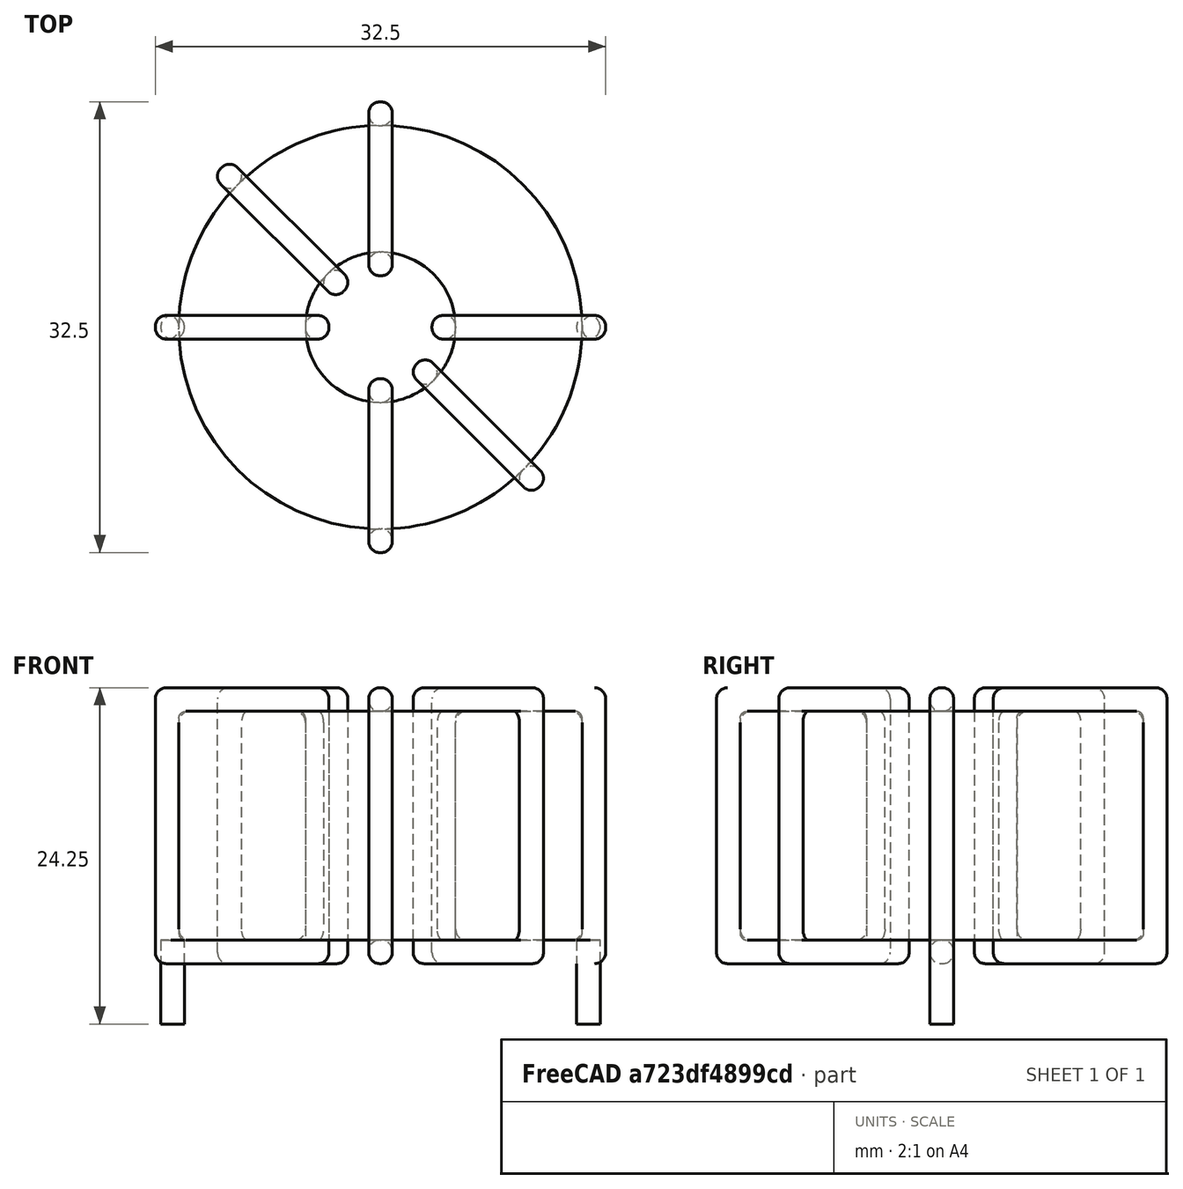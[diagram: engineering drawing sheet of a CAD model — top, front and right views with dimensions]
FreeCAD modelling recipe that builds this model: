
FCSTD DOCUMENT  (FreeCAD 0.16R6703 (Git))
Label: L_Toroid_Horizontal_D32.5mm_P30.00mm_Bourns_2300series
License: All rights reserved
LicenseURL: http://en.wikipedia.org/wiki/All_rights_reserved
objects: Sketcher::SketchObject×6, PartDesign::Pad×6, PartDesign::Fillet×5, Spreadsheet::Sheet×1
note: 23 computed .brp shape members not serialized (recipe doc carries the construction recipe); baked Part::Feature solids carry a one-line shape summary decoded from their .brp

FEATURE [Spreadsheet::Sheet] Spreadsheet  label="dimensions"
  cells = A1=Wx; B1(Wx)=32.5; C1(WW)=10.83333333333333; D1=32.5; A2=Wy; B2(Wy)=32.5; D2=32.5; A3=RM; B3(RMx)=30; C3(RMy)=0; A4=d_wire; B4(d_wire)=1.7; A5=H; B5(H)=16.5; A6=offsetx; B6(offsetx)=1.25
FEATURE [Sketcher::SketchObject] Sketch
  Placement = pos=(0,0,2.2) rot=(0,0,1;0rad)
  expr: Placement.Base.z = 0.5 + Spreadsheet.d_wire
  expr: Constraints[0] = Spreadsheet.Wx / 2 - Spreadsheet.d_wire
  expr: Constraints[4] = Spreadsheet.WW / 2
  expr: Constraints[2] = Spreadsheet.RMy / 2
  expr: Constraints[1] = Spreadsheet.RMx / 2
  sketch-geometry (2):
    g0: Circle CenterX=15 CenterY=0 CenterZ=0 NormalX=0 NormalY=0 NormalZ=1 Radius=14.55
    g1: Circle CenterX=15 CenterY=0 CenterZ=0 NormalX=0 NormalY=0 NormalZ=1 Radius=5.41667
  constraints (5):
    c: Radius(g0) = 14.55
    c: DistanceX(g-1,g0) = 15
    c: DistanceY(g-1,g0) = 0
    c: Coincident(g1,g0)
    c: Radius(g1) = 5.41667
FEATURE [PartDesign::Pad] Pad
  Length = 16.5
  Length2 = 100
  Placement = pos=(0,0,2.2) rot=(0,0,1;0rad)
  Sketch = -> Sketch
  Type = 0
  expr: Length = Spreadsheet.H
FEATURE [Sketcher::SketchObject] Sketch001
  Placement = pos=(0,0,1.35) rot=(0,0,1;0rad)
  expr: Placement.Base.z = 0.5 + Spreadsheet.d_wire * 0.5
  expr: Constraints[4] = Spreadsheet.RMx
  expr: Constraints[2] = Spreadsheet.RMy
  expr: Constraints[1] = Spreadsheet.d_wire / 2
  sketch-geometry (2):
    g0: Circle CenterX=0 CenterY=0 CenterZ=0 NormalX=0 NormalY=0 NormalZ=1 Radius=0.85
    g1: Circle CenterX=30 CenterY=0 CenterZ=0 NormalX=0 NormalY=0 NormalZ=1 Radius=0.85
  constraints (5):
    c: Equal(g0,g1)
    c: Radius(g0) = 0.85
    c: DistanceY(g-1,g1) = 0
    c: Coincident(g0,g-1)
    c: DistanceX(g-1,g1) = 30
FEATURE [PartDesign::Pad] Pad001
  Length = 0.85
  Length2 = 5.2
  Placement = pos=(0,0,1.35) rot=(0,0,1;0rad)
  Reversed = true
  Sketch = -> Sketch001
  Type = 4
  expr: Length2 = 3.5 + Spreadsheet.d_wire
  expr: Length = Spreadsheet.d_wire / 2
FEATURE [PartDesign::Fillet] Fillet
  Base = -> Pad [Edge6,Edge3,Edge2]
  Placement = pos=(0,0,2.2) rot=(0,0,1;0rad)
  Radius = 0.5
FEATURE [Sketcher::SketchObject] Sketch003
  Placement = pos=(15,0,0) rot=(1,0,0;1.5708rad)
  expr: Placement.Base.x = Spreadsheet.RMx / 2
  expr: Constraints[49] = Spreadsheet.Wx - Spreadsheet.d_wire * 2
  expr: Constraints[44] = Spreadsheet.d_wire
  expr: Constraints[23] = Spreadsheet.H
  expr: Constraints[22] = Spreadsheet.Wx / 2 - Spreadsheet.d_wire
  expr: Placement.Base.y = Spreadsheet.RMy / 2
  expr: Constraints[21] = (Spreadsheet.Wx - Spreadsheet.WW) / 2 - Spreadsheet.d_wire
  expr: Constraints[19] = Spreadsheet.d_wire
  expr: Constraints[17] = Spreadsheet.d_wire
  expr: Constraints[18] = Spreadsheet.d_wire
  expr: Constraints[16] = Spreadsheet.d_wire
  sketch-geometry (16):
    g0: LineSegment StartX=-3.71667 StartY=0.5 StartZ=0 EndX=-16.25 EndY=0.5 EndZ=0
    g1: LineSegment StartX=-16.25 StartY=0.5 StartZ=0 EndX=-16.25 EndY=20.4 EndZ=0
    g2: LineSegment StartX=-16.25 StartY=20.4 StartZ=0 EndX=-3.71667 EndY=20.4 EndZ=0
    g3: LineSegment StartX=-3.71667 StartY=20.4 StartZ=0 EndX=-3.71667 EndY=0.5 EndZ=0
    g4: LineSegment StartX=-14.55 StartY=18.7 StartZ=0 EndX=-5.41667 EndY=18.7 EndZ=0
    g5: LineSegment StartX=-5.41667 StartY=18.7 StartZ=0 EndX=-5.41667 EndY=2.2 EndZ=0
    g6: LineSegment StartX=-5.41667 StartY=2.2 StartZ=0 EndX=-14.55 EndY=2.2 EndZ=0
    g7: LineSegment StartX=-14.55 StartY=2.2 StartZ=0 EndX=-14.55 EndY=18.7 EndZ=0
    g8: LineSegment StartX=3.71667 StartY=20.4 StartZ=0 EndX=16.25 EndY=20.4 EndZ=0
    g9: LineSegment StartX=16.25 StartY=20.4 StartZ=0 EndX=16.25 EndY=0.5 EndZ=0
    g10: LineSegment StartX=16.25 StartY=0.5 StartZ=0 EndX=3.71667 EndY=0.5 EndZ=0
    g11: LineSegment StartX=3.71667 StartY=0.5 StartZ=0 EndX=3.71667 EndY=20.4 EndZ=0
    g12: LineSegment StartX=5.41667 StartY=18.7 StartZ=0 EndX=14.55 EndY=18.7 EndZ=0
    g13: LineSegment StartX=14.55 StartY=18.7 StartZ=0 EndX=14.55 EndY=2.2 EndZ=0
    g14: LineSegment StartX=14.55 StartY=2.2 StartZ=0 EndX=5.41667 EndY=2.2 EndZ=0
    g15: LineSegment StartX=5.41667 StartY=2.2 StartZ=0 EndX=5.41667 EndY=18.7 EndZ=0
  constraints (50):
    c: Horizontal(g0)
    c: Coincident(g1,g0)
    c: Vertical(g1)
    c: Coincident(g2,g1)
    c: Horizontal(g2)
    c: Coincident(g3,g2)
    c: Coincident(g3,g0)
    c: Vertical(g3)
    c: Coincident(g4,g5)
    c: Coincident(g5,g6)
    c: Coincident(g6,g7)
    c: Coincident(g7,g4)
    c: Horizontal(g4)
    c: Horizontal(g6)
    c: Vertical(g5)
    c: Vertical(g7)
    c: DistanceX(g1,g4) = 1.7
    c: DistanceY(g4,g1) = 1.7
    c: DistanceX(g5,g0) = 1.7
    c: DistanceY(g0,g5) = 1.7
    c: DistanceY(g-1,g0) = 0.5
    c: DistanceX(g6,g6) = 9.13333
    c: DistanceX(g6,g-1) = 14.55
    c: DistanceY(g7,g7) = 16.5
    c: Coincident(g8,g9)
    c: Coincident(g9,g10)
    c: Coincident(g10,g11)
    c: Coincident(g11,g8)
    c: Horizontal(g8)
    c: Horizontal(g10)
    c: Vertical(g9)
    c: Vertical(g11)
    c: Coincident(g12,g13)
    c: Coincident(g13,g14)
    c: Coincident(g14,g15)
    c: Coincident(g15,g12)
    c: Horizontal(g12)
    c: Horizontal(g14)
    c: Vertical(g13)
    c: Vertical(g15)
    c: DistanceY(g8,g2) = 0
    c: DistanceY(g10,g0) = 0
    c: DistanceY(g14,g5) = 0
    c: DistanceY(g12,g4) = 0
    c: DistanceX(g8,g12) = 1.7
    c: Equal(g8,g2)
    c: Equal(g12,g4)
    c: Equal(g9,g1)
    c: Equal(g13,g7)
    c: DistanceX(g4,g12) = 29.1
FEATURE [PartDesign::Pad] Pad002
  Length = 1.7
  Length2 = 100
  Midplane = true
  Placement = pos=(15,0,0) rot=(1,0,0;1.5708rad)
  Sketch = -> Sketch003
  Type = 0
  expr: Length = Spreadsheet.d_wire
FEATURE [PartDesign::Fillet] Fillet001
  Base = -> Pad002 [Edge38,Edge41,Edge42,Edge43,Edge29,Edge32,Edge33,Edge34,Edge25,Edge35,Edge36,Edge13,Edge14,Edge15,Edge16,Edge17,Edge18,Edge19,Edge1,Edge2,Edge3,Edge4,Edge5,Edge6,Edge7,Edge37,Edge39,Edge40,Edge20,Edge23,Edge24,Edge21,Edge22,Edge8,Edge9,Edge10,Edge11,Edge12,Edge26,Edge27,+8 more]
  Placement = pos=(15,0,0) rot=(1,0,0;1.5708rad)
  Radius = 0.799
  expr: Radius = Spreadsheet.d_wire * 0.47
FEATURE [Sketcher::SketchObject] Sketch004
  Placement = pos=(15,0,0) rot=(0.862856,0.357407,0.357407;1.71777rad)
  expr: Placement.Base.x = Spreadsheet.RMx / 2
  expr: Constraints[49] = Spreadsheet.Wx - 2 * Spreadsheet.d_wire
  expr: Constraints[44] = Spreadsheet.d_wire
  expr: Constraints[23] = Spreadsheet.H
  expr: Constraints[22] = Spreadsheet.Wx / 2 - Spreadsheet.d_wire
  expr: Placement.Base.y = Spreadsheet.RMy / 2
  expr: Constraints[21] = (Spreadsheet.Wx - Spreadsheet.WW) / 2 - Spreadsheet.d_wire
  expr: Constraints[19] = Spreadsheet.d_wire
  expr: Constraints[17] = Spreadsheet.d_wire
  expr: Constraints[18] = Spreadsheet.d_wire
  expr: Constraints[16] = Spreadsheet.d_wire
  sketch-geometry (16):
    g0: LineSegment StartX=-3.71667 StartY=0.5 StartZ=0 EndX=-16.25 EndY=0.5 EndZ=0
    g1: LineSegment StartX=-16.25 StartY=0.5 StartZ=0 EndX=-16.25 EndY=20.4 EndZ=0
    g2: LineSegment StartX=-16.25 StartY=20.4 StartZ=0 EndX=-3.71667 EndY=20.4 EndZ=0
    g3: LineSegment StartX=-3.71667 StartY=20.4 StartZ=0 EndX=-3.71667 EndY=0.5 EndZ=0
    g4: LineSegment StartX=-14.55 StartY=18.7 StartZ=0 EndX=-5.41667 EndY=18.7 EndZ=0
    g5: LineSegment StartX=-5.41667 StartY=18.7 StartZ=0 EndX=-5.41667 EndY=2.2 EndZ=0
    g6: LineSegment StartX=-5.41667 StartY=2.2 StartZ=0 EndX=-14.55 EndY=2.2 EndZ=0
    g7: LineSegment StartX=-14.55 StartY=2.2 StartZ=0 EndX=-14.55 EndY=18.7 EndZ=0
    g8: LineSegment StartX=3.71667 StartY=20.4 StartZ=0 EndX=16.25 EndY=20.4 EndZ=0
    g9: LineSegment StartX=16.25 StartY=20.4 StartZ=0 EndX=16.25 EndY=0.5 EndZ=0
    g10: LineSegment StartX=16.25 StartY=0.5 StartZ=0 EndX=3.71667 EndY=0.5 EndZ=0
    g11: LineSegment StartX=3.71667 StartY=0.5 StartZ=0 EndX=3.71667 EndY=20.4 EndZ=0
    g12: LineSegment StartX=5.41667 StartY=18.7 StartZ=0 EndX=14.55 EndY=18.7 EndZ=0
    g13: LineSegment StartX=14.55 StartY=18.7 StartZ=0 EndX=14.55 EndY=2.2 EndZ=0
    g14: LineSegment StartX=14.55 StartY=2.2 StartZ=0 EndX=5.41667 EndY=2.2 EndZ=0
    g15: LineSegment StartX=5.41667 StartY=2.2 StartZ=0 EndX=5.41667 EndY=18.7 EndZ=0
  constraints (50):
    c: Horizontal(g0)
    c: Coincident(g1,g0)
    c: Vertical(g1)
    c: Coincident(g2,g1)
    c: Horizontal(g2)
    c: Coincident(g3,g2)
    c: Coincident(g3,g0)
    c: Vertical(g3)
    c: Coincident(g4,g5)
    c: Coincident(g5,g6)
    c: Coincident(g6,g7)
    c: Coincident(g7,g4)
    c: Horizontal(g4)
    c: Horizontal(g6)
    c: Vertical(g5)
    c: Vertical(g7)
    c: DistanceX(g1,g4) = 1.7
    c: DistanceY(g4,g1) = 1.7
    c: DistanceX(g5,g0) = 1.7
    c: DistanceY(g0,g5) = 1.7
    c: DistanceY(g-1,g0) = 0.5
    c: DistanceX(g6,g6) = 9.13333
    c: DistanceX(g6,g-1) = 14.55
    c: DistanceY(g7,g7) = 16.5
    c: Coincident(g8,g9)
    c: Coincident(g9,g10)
    c: Coincident(g10,g11)
    c: Coincident(g11,g8)
    c: Horizontal(g8)
    c: Horizontal(g10)
    c: Vertical(g9)
    c: Vertical(g11)
    c: Coincident(g12,g13)
    c: Coincident(g13,g14)
    c: Coincident(g14,g15)
    c: Coincident(g15,g12)
    c: Horizontal(g12)
    c: Horizontal(g14)
    c: Vertical(g13)
    c: Vertical(g15)
    c: DistanceY(g8,g2) = 0
    c: DistanceY(g10,g0) = 0
    c: DistanceY(g14,g5) = 0
    c: DistanceY(g12,g4) = 0
    c: DistanceX(g8,g12) = 1.7
    c: Equal(g8,g2)
    c: Equal(g12,g4)
    c: Equal(g9,g1)
    c: Equal(g13,g7)
    c: DistanceX(g4,g12) = 29.1
FEATURE [PartDesign::Pad] Pad003
  Length = 1.7
  Length2 = 100
  Midplane = true
  Placement = pos=(15,0,0) rot=(0.862856,0.357407,0.357407;1.71777rad)
  Sketch = -> Sketch004
  Type = 0
  expr: Length = Spreadsheet.d_wire
FEATURE [PartDesign::Fillet] Fillet002
  Base = -> Pad003 [Edge38,Edge41,Edge42,Edge43,Edge29,Edge32,Edge33,Edge34,Edge25,Edge35,Edge36,Edge13,Edge14,Edge15,Edge16,Edge17,Edge18,Edge19,Edge1,Edge2,Edge3,Edge4,Edge5,Edge6,Edge7,Edge37,Edge39,Edge40,Edge20,Edge23,Edge24,Edge21,Edge22,Edge8,Edge9,Edge10,Edge11,Edge12,Edge26,Edge27,+8 more]
  Placement = pos=(15,0,0) rot=(0.862856,0.357407,0.357407;1.71777rad)
  Radius = 0.799
  expr: Radius = Spreadsheet.d_wire * 0.47
FEATURE [Sketcher::SketchObject] Sketch005
  Placement = pos=(15,0,0) rot=(0.862856,-0.357407,-0.357407;1.71777rad)
  expr: Placement.Base.x = Spreadsheet.RMx / 2
  expr: Constraints[49] = Spreadsheet.Wx - 2 * Spreadsheet.d_wire
  expr: Constraints[44] = Spreadsheet.d_wire
  expr: Constraints[23] = Spreadsheet.H
  expr: Constraints[22] = Spreadsheet.Wx / 2 - Spreadsheet.d_wire
  expr: Placement.Base.y = Spreadsheet.RMy / 2
  expr: Constraints[21] = (Spreadsheet.Wx - Spreadsheet.WW) / 2 - Spreadsheet.d_wire
  expr: Constraints[19] = Spreadsheet.d_wire
  expr: Constraints[17] = Spreadsheet.d_wire
  expr: Constraints[18] = Spreadsheet.d_wire
  expr: Constraints[16] = Spreadsheet.d_wire
  sketch-geometry (16):
    g0: LineSegment StartX=-3.71667 StartY=0.5 StartZ=0 EndX=-16.25 EndY=0.5 EndZ=0
    g1: LineSegment StartX=-16.25 StartY=0.5 StartZ=0 EndX=-16.25 EndY=20.4 EndZ=0
    g2: LineSegment StartX=-16.25 StartY=20.4 StartZ=0 EndX=-3.71667 EndY=20.4 EndZ=0
    g3: LineSegment StartX=-3.71667 StartY=20.4 StartZ=0 EndX=-3.71667 EndY=0.5 EndZ=0
    g4: LineSegment StartX=-14.55 StartY=18.7 StartZ=0 EndX=-5.41667 EndY=18.7 EndZ=0
    g5: LineSegment StartX=-5.41667 StartY=18.7 StartZ=0 EndX=-5.41667 EndY=2.2 EndZ=0
    g6: LineSegment StartX=-5.41667 StartY=2.2 StartZ=0 EndX=-14.55 EndY=2.2 EndZ=0
    g7: LineSegment StartX=-14.55 StartY=2.2 StartZ=0 EndX=-14.55 EndY=18.7 EndZ=0
    g8: LineSegment StartX=3.71667 StartY=20.4 StartZ=0 EndX=16.25 EndY=20.4 EndZ=0
    g9: LineSegment StartX=16.25 StartY=20.4 StartZ=0 EndX=16.25 EndY=0.5 EndZ=0
    g10: LineSegment StartX=16.25 StartY=0.5 StartZ=0 EndX=3.71667 EndY=0.5 EndZ=0
    g11: LineSegment StartX=3.71667 StartY=0.5 StartZ=0 EndX=3.71667 EndY=20.4 EndZ=0
    g12: LineSegment StartX=5.41667 StartY=18.7 StartZ=0 EndX=14.55 EndY=18.7 EndZ=0
    g13: LineSegment StartX=14.55 StartY=18.7 StartZ=0 EndX=14.55 EndY=2.2 EndZ=0
    g14: LineSegment StartX=14.55 StartY=2.2 StartZ=0 EndX=5.41667 EndY=2.2 EndZ=0
    g15: LineSegment StartX=5.41667 StartY=2.2 StartZ=0 EndX=5.41667 EndY=18.7 EndZ=0
  constraints (50):
    c: Horizontal(g0)
    c: Coincident(g1,g0)
    c: Vertical(g1)
    c: Coincident(g2,g1)
    c: Horizontal(g2)
    c: Coincident(g3,g2)
    c: Coincident(g3,g0)
    c: Vertical(g3)
    c: Coincident(g4,g5)
    c: Coincident(g5,g6)
    c: Coincident(g6,g7)
    c: Coincident(g7,g4)
    c: Horizontal(g4)
    c: Horizontal(g6)
    c: Vertical(g5)
    c: Vertical(g7)
    c: DistanceX(g1,g4) = 1.7
    c: DistanceY(g4,g1) = 1.7
    c: DistanceX(g5,g0) = 1.7
    c: DistanceY(g0,g5) = 1.7
    c: DistanceY(g-1,g0) = 0.5
    c: DistanceX(g6,g6) = 9.13333
    c: DistanceX(g6,g-1) = 14.55
    c: DistanceY(g7,g7) = 16.5
    c: Coincident(g8,g9)
    c: Coincident(g9,g10)
    c: Coincident(g10,g11)
    c: Coincident(g11,g8)
    c: Horizontal(g8)
    c: Horizontal(g10)
    c: Vertical(g9)
    c: Vertical(g11)
    c: Coincident(g12,g13)
    c: Coincident(g13,g14)
    c: Coincident(g14,g15)
    c: Coincident(g15,g12)
    c: Horizontal(g12)
    c: Horizontal(g14)
    c: Vertical(g13)
    c: Vertical(g15)
    c: DistanceY(g8,g2) = 0
    c: DistanceY(g10,g0) = 0
    c: DistanceY(g14,g5) = 0
    c: DistanceY(g12,g4) = 0
    c: DistanceX(g8,g12) = 1.7
    c: Equal(g8,g2)
    c: Equal(g12,g4)
    c: Equal(g9,g1)
    c: Equal(g13,g7)
    c: DistanceX(g4,g12) = 29.1
FEATURE [PartDesign::Pad] Pad004
  Length = 1.7
  Length2 = 100
  Midplane = true
  Placement = pos=(15,0,0) rot=(0.862856,-0.357407,-0.357407;1.71777rad)
  Sketch = -> Sketch005
  Type = 0
  expr: Length = Spreadsheet.d_wire
FEATURE [PartDesign::Fillet] Fillet003
  Base = -> Pad004 [Edge38,Edge41,Edge42,Edge43,Edge29,Edge32,Edge33,Edge34,Edge25,Edge35,Edge36,Edge13,Edge14,Edge15,Edge16,Edge17,Edge18,Edge19,Edge1,Edge2,Edge3,Edge4,Edge5,Edge6,Edge7,Edge37,Edge39,Edge40,Edge20,Edge23,Edge24,Edge21,Edge22,Edge8,Edge9,Edge10,Edge11,Edge12,Edge26,Edge27,+8 more]
  Placement = pos=(15,0,0) rot=(0.862856,-0.357407,-0.357407;1.71777rad)
  Radius = 0.799
  expr: Radius = Spreadsheet.d_wire * 0.47
FEATURE [Sketcher::SketchObject] Sketch006
  Placement = pos=(15,0,0) rot=(0.57735,0.57735,0.57735;2.0944rad)
  expr: Placement.Base.x = Spreadsheet.RMx / 2
  expr: Constraints[49] = Spreadsheet.Wx - Spreadsheet.d_wire * 2
  expr: Constraints[44] = Spreadsheet.d_wire
  expr: Constraints[23] = Spreadsheet.H
  expr: Constraints[22] = Spreadsheet.Wx / 2 - Spreadsheet.d_wire
  expr: Placement.Base.y = Spreadsheet.RMy / 2
  expr: Constraints[21] = (Spreadsheet.Wx - Spreadsheet.WW) / 2 - Spreadsheet.d_wire
  expr: Constraints[19] = Spreadsheet.d_wire
  expr: Constraints[17] = Spreadsheet.d_wire
  expr: Constraints[18] = Spreadsheet.d_wire
  expr: Constraints[16] = Spreadsheet.d_wire
  sketch-geometry (16):
    g0: LineSegment StartX=-3.71667 StartY=0.5 StartZ=0 EndX=-16.25 EndY=0.5 EndZ=0
    g1: LineSegment StartX=-16.25 StartY=0.5 StartZ=0 EndX=-16.25 EndY=20.4 EndZ=0
    g2: LineSegment StartX=-16.25 StartY=20.4 StartZ=0 EndX=-3.71667 EndY=20.4 EndZ=0
    g3: LineSegment StartX=-3.71667 StartY=20.4 StartZ=0 EndX=-3.71667 EndY=0.5 EndZ=0
    g4: LineSegment StartX=-14.55 StartY=18.7 StartZ=0 EndX=-5.41667 EndY=18.7 EndZ=0
    g5: LineSegment StartX=-5.41667 StartY=18.7 StartZ=0 EndX=-5.41667 EndY=2.2 EndZ=0
    g6: LineSegment StartX=-5.41667 StartY=2.2 StartZ=0 EndX=-14.55 EndY=2.2 EndZ=0
    g7: LineSegment StartX=-14.55 StartY=2.2 StartZ=0 EndX=-14.55 EndY=18.7 EndZ=0
    g8: LineSegment StartX=3.71667 StartY=20.4 StartZ=0 EndX=16.25 EndY=20.4 EndZ=0
    g9: LineSegment StartX=16.25 StartY=20.4 StartZ=0 EndX=16.25 EndY=0.5 EndZ=0
    g10: LineSegment StartX=16.25 StartY=0.5 StartZ=0 EndX=3.71667 EndY=0.5 EndZ=0
    g11: LineSegment StartX=3.71667 StartY=0.5 StartZ=0 EndX=3.71667 EndY=20.4 EndZ=0
    g12: LineSegment StartX=5.41667 StartY=18.7 StartZ=0 EndX=14.55 EndY=18.7 EndZ=0
    g13: LineSegment StartX=14.55 StartY=18.7 StartZ=0 EndX=14.55 EndY=2.2 EndZ=0
    g14: LineSegment StartX=14.55 StartY=2.2 StartZ=0 EndX=5.41667 EndY=2.2 EndZ=0
    g15: LineSegment StartX=5.41667 StartY=2.2 StartZ=0 EndX=5.41667 EndY=18.7 EndZ=0
  constraints (50):
    c: Horizontal(g0)
    c: Coincident(g1,g0)
    c: Vertical(g1)
    c: Coincident(g2,g1)
    c: Horizontal(g2)
    c: Coincident(g3,g2)
    c: Coincident(g3,g0)
    c: Vertical(g3)
    c: Coincident(g4,g5)
    c: Coincident(g5,g6)
    c: Coincident(g6,g7)
    c: Coincident(g7,g4)
    c: Horizontal(g4)
    c: Horizontal(g6)
    c: Vertical(g5)
    c: Vertical(g7)
    c: DistanceX(g1,g4) = 1.7
    c: DistanceY(g4,g1) = 1.7
    c: DistanceX(g5,g0) = 1.7
    c: DistanceY(g0,g5) = 1.7
    c: DistanceY(g-1,g0) = 0.5
    c: DistanceX(g6,g6) = 9.13333
    c: DistanceX(g6,g-1) = 14.55
    c: DistanceY(g7,g7) = 16.5
    c: Coincident(g8,g9)
    c: Coincident(g9,g10)
    c: Coincident(g10,g11)
    c: Coincident(g11,g8)
    c: Horizontal(g8)
    c: Horizontal(g10)
    c: Vertical(g9)
    c: Vertical(g11)
    c: Coincident(g12,g13)
    c: Coincident(g13,g14)
    c: Coincident(g14,g15)
    c: Coincident(g15,g12)
    c: Horizontal(g12)
    c: Horizontal(g14)
    c: Vertical(g13)
    c: Vertical(g15)
    c: DistanceY(g8,g2) = 0
    c: DistanceY(g10,g0) = 0
    c: DistanceY(g14,g5) = 0
    c: DistanceY(g12,g4) = 0
    c: DistanceX(g8,g12) = 1.7
    c: Equal(g8,g2)
    c: Equal(g12,g4)
    c: Equal(g9,g1)
    c: Equal(g13,g7)
    c: DistanceX(g4,g12) = 29.1
FEATURE [PartDesign::Pad] Pad005
  Length = 1.7
  Length2 = 100
  Midplane = true
  Placement = pos=(15,0,0) rot=(0.57735,0.57735,0.57735;2.0944rad)
  Sketch = -> Sketch006
  Type = 0
  expr: Length = Spreadsheet.d_wire
FEATURE [PartDesign::Fillet] Fillet004
  Base = -> Pad005 [Edge38,Edge41,Edge42,Edge43,Edge29,Edge32,Edge33,Edge34,Edge25,Edge35,Edge36,Edge13,Edge14,Edge15,Edge16,Edge17,Edge18,Edge19,Edge1,Edge2,Edge3,Edge4,Edge5,Edge6,Edge7,Edge37,Edge39,Edge40,Edge20,Edge23,Edge24,Edge21,Edge22,Edge8,Edge9,Edge10,Edge11,Edge12,Edge26,Edge27,+8 more]
  Placement = pos=(15,0,0) rot=(0.57735,0.57735,0.57735;2.0944rad)
  Radius = 0.799
  expr: Radius = Spreadsheet.d_wire * 0.47
